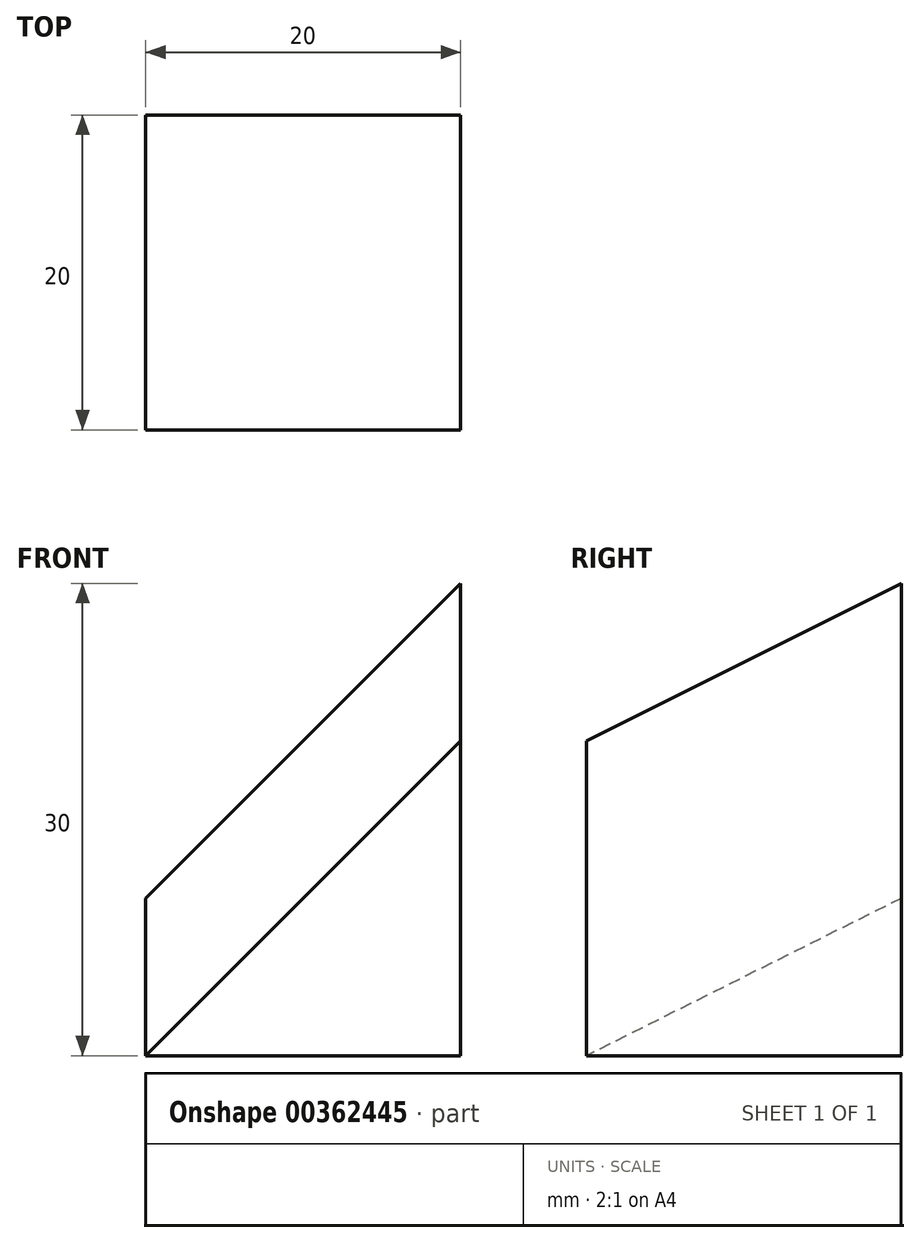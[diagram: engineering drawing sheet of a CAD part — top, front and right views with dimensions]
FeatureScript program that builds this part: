
annotation { "Feature Type Name" : "Feature", "Feature Type Description" : "" }
export const myFeature = defineFeature(function(context is Context, id is Id, definition is map)
    precondition{}
    {
        {
            var Q0;
            Q0=qCreatedBy(makeId("Front.planeOp"),FACE);
            var sketch = newSketch(context, id + "F0", { "sketchPlane" : qUnion([Q0])});
            skLineSegment(sketch, "E0.bottom", {"start": v(0, 0) * mm, "end": v(-20, 0) * mm});
            skLineSegment(sketch, "E0.top", {"start": v(0, 30) * mm, "end": v(-20, 30) * mm});
            skLineSegment(sketch, "E0.left", {"start": v(0, 0) * mm, "end": v(0, 30) * mm});
            skLineSegment(sketch, "E0.right", {"start": v(-20, 0) * mm, "end": v(-20, 30) * mm});
            skSolve(sketch);
        }
        {
            var Q0;
            Q0 = qSketchRegion(id + "F0", true);
            extrude(context, id + "F1", {"entities" : qUnion([Q0]), "depth" : 20 * mm});
        }
        {
            var Q0;
            Q0=makeQuery(id+"F1.opExtrude","SWEPT_FACE",FACE,{"disambiguationData":[OSD([sQuery(id+"F0.wireOp",EDGE,"E0.left")])]});
            var sketch = newSketch(context, id + "F2", { "sketchPlane" : qUnion([Q0])});
            skLineSegment(sketch, "E1", {"start": v(0, 30) * mm, "end": v(-20, 20) * mm});
            skSolve(sketch);
        }
        {
            var Q0;
            Q0=makeQuery(id+"F1.opExtrude","CAP_FACE",FACE,{"disambiguationData":[OSD([sQuery(id+"F0.wireOp",EDGE,"E0.bottom"),sQuery(id+"F0.wireOp",EDGE,"E0.top"),sQuery(id+"F0.wireOp",EDGE,"E0.left"),sQuery(id+"F0.wireOp",EDGE,"E0.right")])],"isStart":false});
            var sketch = newSketch(context, id + "F3", { "sketchPlane" : qUnion([Q0])});
            skLineSegment(sketch, "E2", {"start": v(0, 20) * mm, "end": v(-20, 0) * mm});
            skSolve(sketch);
        }
        {
            var Q0;
            Q0=sQuery(id+"F2.wireOp",VERTEX,"E1.start");
            var Q1;
            Q1=sQuery(id+"F3.wireOp",VERTEX,"E2.start");
            var Q2;
            Q2=sQuery(id+"F3.wireOp",VERTEX,"E2.end");
            cPlane(context, id + "F4", {"entities" : qUnion([Q0, Q1, Q2]), "cplaneType" : CPlaneType.THREE_POINT, "offset" : 25 * mm, "width" : 150 * mm, "height" : 150 * mm});
        }
        {
            var Q0;
            Q0=makeQuery(id+"F1.opExtrude","SWEPT_FACE",FACE,{"disambiguationData":[OSD([sQuery(id+"F0.wireOp",EDGE,"E0.top")])]});
            var Q1;
            Q1=qCreatedBy(id+"F4.planeOp",FACE);
            extrude(context, id + "F5", {"entities" : qUnion([Q0]), "operationType" : NewBodyOperationType.REMOVE, "endBound" : BoundingType.UP_TO_SURFACE, "oppositeDirection" : true, "endBoundEntityFace" : qUnion([Q1]), "depth" : 25 * mm});
        }
    });
